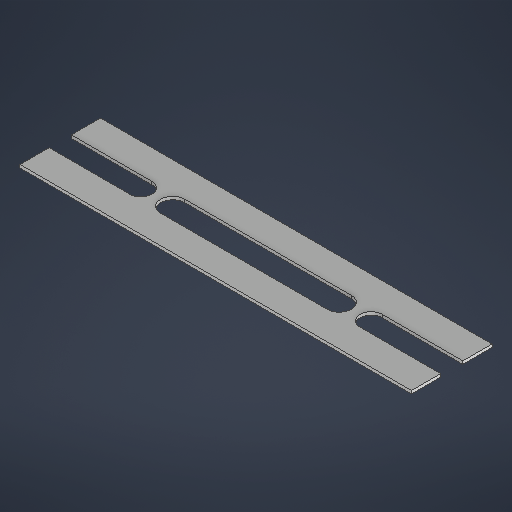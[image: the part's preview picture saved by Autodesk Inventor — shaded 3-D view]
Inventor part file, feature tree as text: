
AUTODESK INVENTOR PART (.ipt)
format: ipt  version: 2025 (Build 290162000, 162)  size: 224,256 bytes
history: native  units: in
note: dims shown in document units (in); Inventor stores cm internally (conversion verified against a paired STEP export)
features: extrude x2, sketch x2
ambient origin geometry x8: Origin, YZ Plane, XZ Plane, XY Plane, X Axis, Y Axis, Z Axis, Center Point
bodies: Body1 (feature_tree)
feature tree (4):
  extrude  "Extrusion5"  Depth=0.7874in TaperAngle=0.0deg
  extrude  "Extrusion7"  Depth=0.0295in
  sketch  "Sketch5"  dims[d24=0.0394in d72=0.7874in d73=0.0in]
  sketch  "Sketch7"  dims[d83=3.8268in d84=0.0295in d85=0.2165in d86=0.2165in d87=0.3937in d88=0.7874in d89=0.7874in d90=0.3937in d91=0.7874in d92=0.0in d93=0.2362in d94=1.1in]
